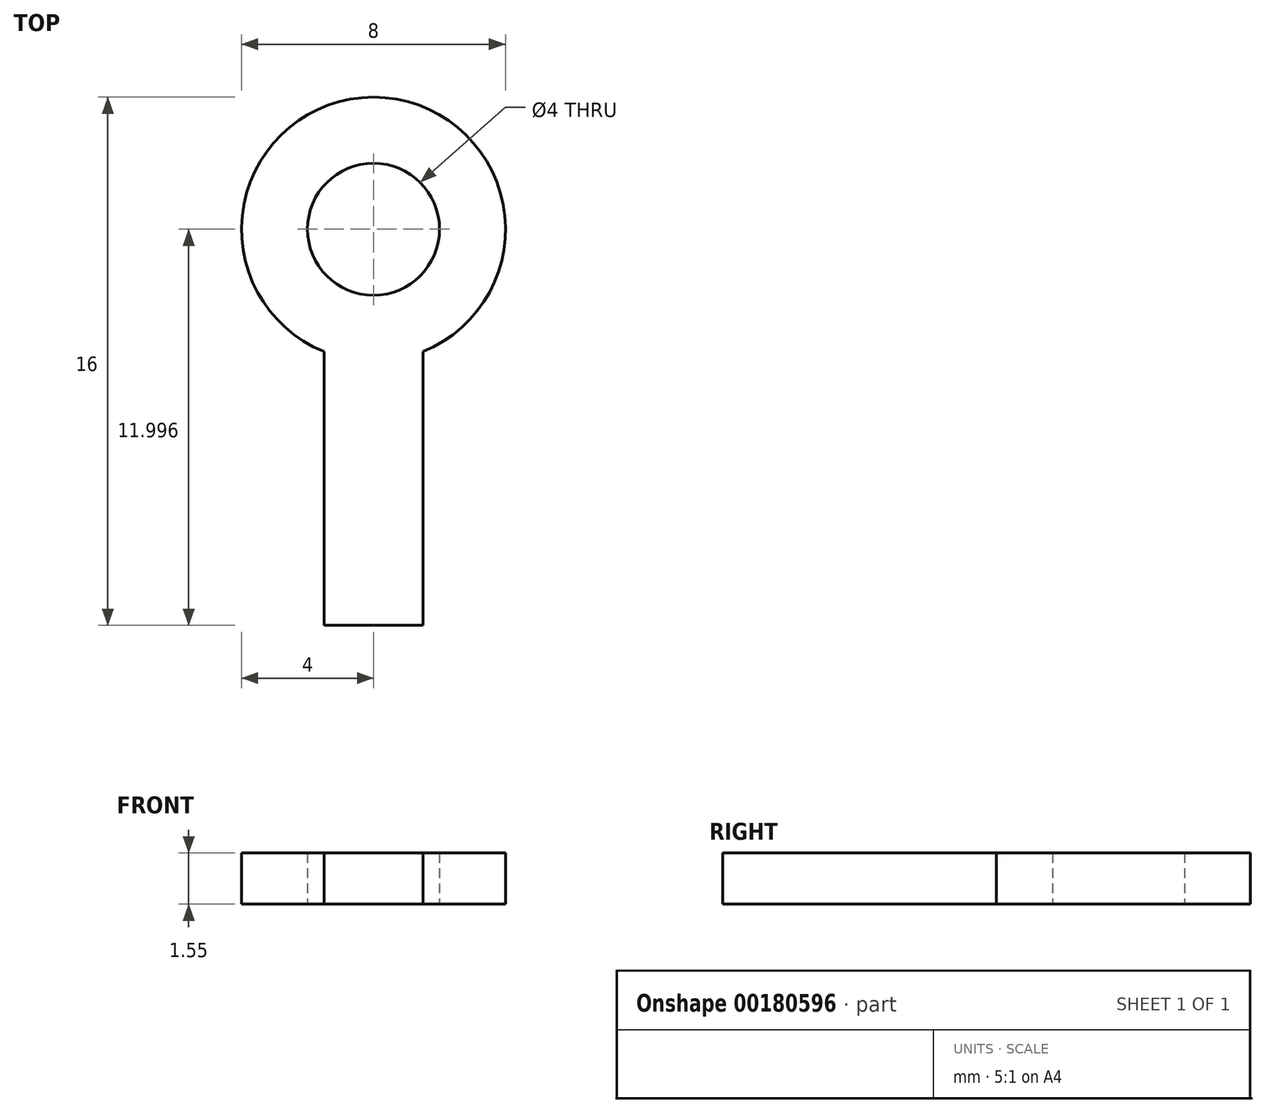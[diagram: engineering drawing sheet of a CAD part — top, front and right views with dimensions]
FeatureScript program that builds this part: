
annotation { "Feature Type Name" : "Feature", "Feature Type Description" : "" }
export const myFeature = defineFeature(function(context is Context, id is Id, definition is map)
    precondition{}
    {
        {
            var Q0;
            Q0=qCreatedBy(makeId("Top.planeOp"),FACE);
            var sketch = newSketch(context, id + "F0", { "sketchPlane" : qUnion([Q0])});
            skCircle(sketch, "E0", {"center": v(0, 26.05) * mm, "radius": 2 * mm});
            skCircle(sketch, "E1", {"center": v(0, 26.05) * mm, "radius": 4 * mm});
            skLineSegment(sketch, "E2.bottom", {"start": v(-1.5, 24.05) * mm, "end": v(1.5, 24.05) * mm});
            skLineSegment(sketch, "E2.left", {"start": v(-1.5, 24.05) * mm, "end": v(-1.5, 14.05) * mm});
            skLineSegment(sketch, "E3", {"start": v(0, 26.05) * mm, "end": v(0, 24.05) * mm});
            skLineSegment(sketch, "E4.bottom", {"start": v(-1.5, 14.05) * mm, "end": v(1.5, 14.05) * mm});
            skLineSegment(sketch, "E5", {"start": v(1.5, 24.05) * mm, "end": v(1.5, 14.05) * mm});
            skSolve(sketch);
        }
        {
            var Q0;
            {var subQ3=sQuery(id+"F0.wireOp",EDGE,"E0");Q0=makeQuery(id+"F0.imprint","IMPRINT",FACE,{"disambiguationData":[TD([[makeQuery(id+"F0.imprint","IMPRINT",EDGE,{"derivedFrom":subQ3}),-1.0]])]});}
            var Q1;
            {var subQ0=sQuery(id+"F0.wireOp",EDGE,"E2.left");var subQ3=sQuery(id+"F0.wireOp",EDGE,"E1");var subQ4=makeQuery(id+"F0.imprint","INTERSECT",VERTEX,{"derivedFrom":[subQ3,subQ0]});Q1=makeQuery(id+"F0.imprint","IMPRINT",FACE,{"disambiguationData":[TD([[makeQuery(id+"F0.imprint","IMPRINT",EDGE,{"disambiguationData":[TD([[subQ4,-1.0]])],"derivedFrom":subQ3}),1.0]])]});}
            var Q2;
            {var subQ5=sQuery(id+"F0.wireOp",EDGE,"E4.bottom");Q2=makeQuery(id+"F0.imprint","IMPRINT",FACE,{"disambiguationData":[TD([[makeQuery(id+"F0.imprint","IMPRINT",EDGE,{"derivedFrom":subQ5}),1.0]])]});}
            extrude(context, id + "F1", {"entities" : qUnion([Q0, Q1, Q2]), "depth" : 1.55 * mm});
        }
    });
